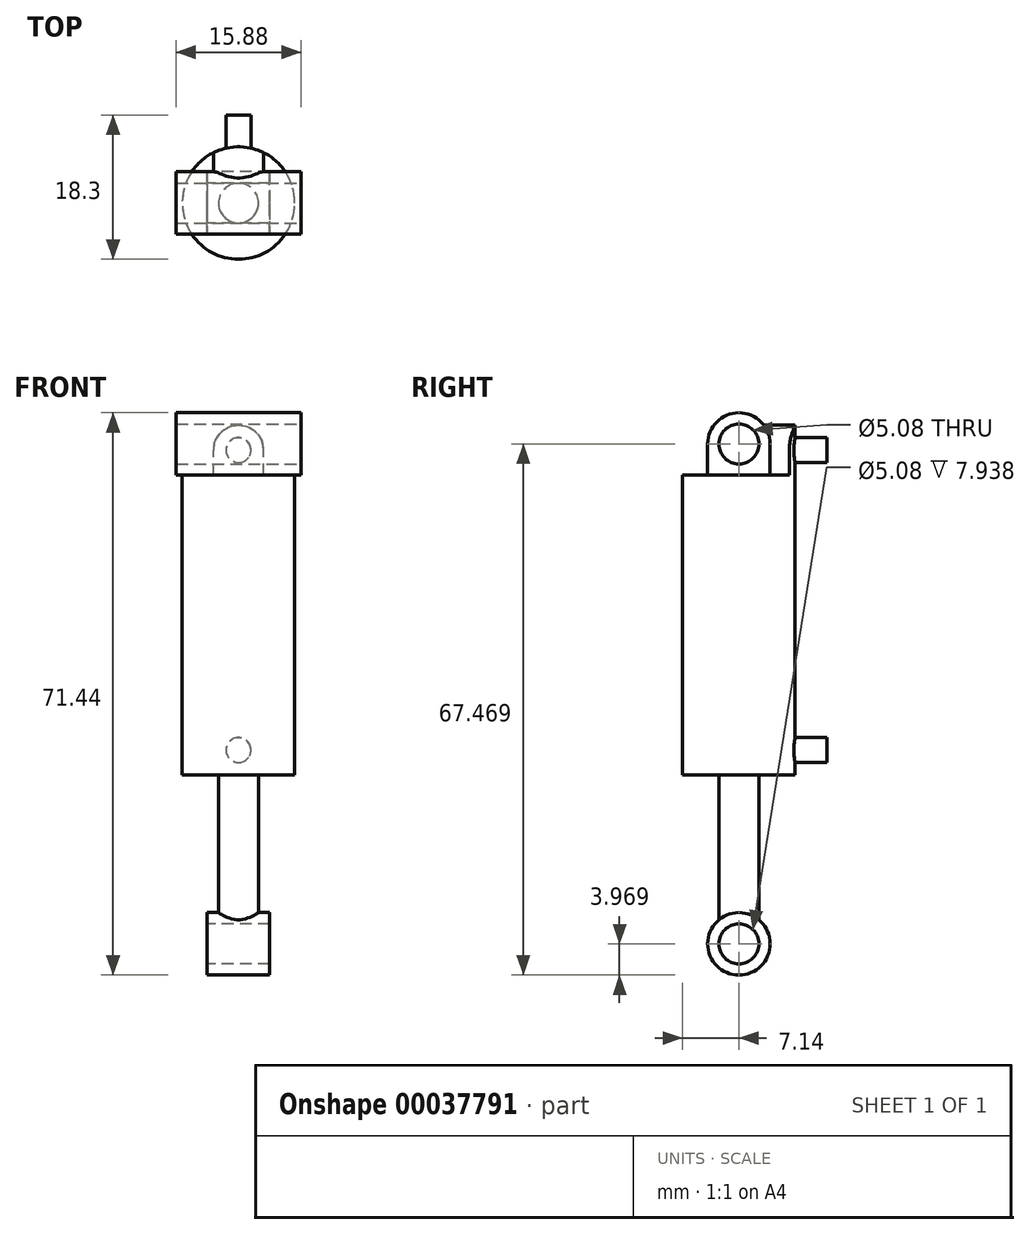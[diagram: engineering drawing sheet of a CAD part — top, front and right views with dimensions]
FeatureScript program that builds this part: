
annotation { "Feature Type Name" : "Feature", "Feature Type Description" : "" }
export const myFeature = defineFeature(function(context is Context, id is Id, definition is map)
    precondition{}
    {
        {
            var Q0;
            Q0=qCreatedBy(makeId("Top.planeOp"),FACE);
            var sketch = newSketch(context, id + "F0", { "sketchPlane" : qUnion([Q0])});
            skCircle(sketch, "E0", {"center": v(0, 0) * mm, "radius": 7.14 * mm});
            skSolve(sketch);
        }
        {
            var Q0;
            Q0 = qSketchRegion(id + "F0", true);
            extrude(context, id + "F1", {"entities" : qUnion([Q0]), "depth" : 38.1 * mm});
        }
        {
            var Q0;
            Q0=makeQuery(id+"F1.opExtrude","CAP_FACE",FACE,{"disambiguationData":[OSD([sQuery(id+"F0.wireOp",EDGE,"E0")])],"isStart":false});
            var sketch = newSketch(context, id + "F2", { "sketchPlane" : qUnion([Q0])});
            skLineSegment(sketch, "E1.rect.bottom", {"start": v(7.94, 3.97) * mm, "end": v(-7.94, 3.97) * mm});
            skLineSegment(sketch, "E1.rect.top", {"start": v(7.94, -3.97) * mm, "end": v(-7.94, -3.97) * mm});
            skLineSegment(sketch, "E1.rect.left", {"start": v(7.94, 3.97) * mm, "end": v(7.94, -3.97) * mm});
            skLineSegment(sketch, "E1.rect.right", {"start": v(-7.94, 3.97) * mm, "end": v(-7.94, -3.97) * mm});
            skPoint(sketch, "E1.rect.middle", {"position": v(0, 0) * mm});
            skSolve(sketch);
        }
        {
            var Q0;
            Q0 = qSketchRegion(id + "F2", true);
            extrude(context, id + "F3", {"entities" : qUnion([Q0]), "operationType" : NewBodyOperationType.ADD, "depth" : 7.94 * mm});
        }
        {
            var Q0;
            Q0=makeQuery(id+"F3.opExtrude","CAP_EDGE",EDGE,{"disambiguationData":[OSD([sQuery(id+"F2.wireOp",EDGE,"E1.rect.bottom")])],"isStart":false});
            var Q1;
            Q1=makeQuery(id+"F3.opExtrude","CAP_EDGE",EDGE,{"disambiguationData":[OSD([sQuery(id+"F2.wireOp",EDGE,"E1.rect.top")])],"isStart":false});
            fillet(context, id + "F4", {"entities" : qUnion([Q0, Q1]), "radius" : 3.97 * mm, "tangentPropagation" : true, "allowEdgeOverflow" : false});
        }
        {
            var Q0;
            Q0=makeQuery(id+"F3.opExtrude","SWEPT_FACE",FACE,{"disambiguationData":[OSD([sQuery(id+"F2.wireOp",EDGE,"E1.rect.left")])]});
            var sketch = newSketch(context, id + "F5", { "sketchPlane" : qUnion([Q0])});
            skCircle(sketch, "E2", {"center": v(0, 42.07) * mm, "radius": 2.54 * mm});
            skSolve(sketch);
        }
        {
            var Q0;
            Q0 = qSketchRegion(id + "F5", true);
            var Q1;
            Q1=makeQuery(id+"F3.opExtrude","SWEPT_FACE",FACE,{"disambiguationData":[OSD([sQuery(id+"F2.wireOp",EDGE,"E1.rect.right")])]});
            extrude(context, id + "F6", {"entities" : qUnion([Q0]), "operationType" : NewBodyOperationType.REMOVE, "endBound" : BoundingType.UP_TO_SURFACE, "oppositeDirection" : true, "endBoundEntityFace" : qUnion([Q1]), "depth" : 25.4 * mm});
        }
        {
            var Q0;
            Q0=makeQuery(id+"F3.opExtrude","SWEPT_FACE",FACE,{"disambiguationData":[OSD([sQuery(id+"F2.wireOp",EDGE,"E1.rect.bottom")])]});
            var sketch = newSketch(context, id + "F7", { "sketchPlane" : qUnion([Q0])});
            skLineSegment(sketch, "E3.bottom", {"start": v(-3.18, 38.1) * mm, "end": v(3.18, 38.1) * mm});
            skLineSegment(sketch, "E3.top", {"start": v(-3.18, 41.27) * mm, "end": v(3.17, 41.27) * mm});
            skLineSegment(sketch, "E3.left", {"start": v(-3.18, 38.1) * mm, "end": v(-3.18, 41.27) * mm});
            skLineSegment(sketch, "E3.right", {"start": v(3.17, 38.1) * mm, "end": v(3.17, 41.27) * mm});
            skPoint(sketch, "E4", {"position": v(0, 38.1) * mm});
            skArc(sketch, "E5", {"start": v(3.17, 41.27) * mm, "mid": v(0, 44.45) * mm, "end": v(-3.18, 41.27) * mm});
            skSolve(sketch);
        }
        {
            var Q0;
            Q0 = qSketchRegion(id + "F7", true);
            var Q1;
            Q1=makeQuery(id+"F1.opExtrude","SWEPT_FACE",FACE,{"disambiguationData":[OSD([sQuery(id+"F0.wireOp",EDGE,"E0")])]});
            var Q2;
            Q2=makeQuery(id+"F4.opFillet","BLEND_FACE",FACE,{"disambiguationData":[OSD([sQuery(id+"F2.wireOp",EDGE,"E1.rect.bottom")])]});
            extrude(context, id + "F8", {"entities" : qUnion([Q0]), "operationType" : NewBodyOperationType.ADD, "endBound" : BoundingType.UP_TO_SURFACE, "endBoundEntityFace" : qUnion([Q1]), "depth" : 25.4 * mm, "hasSecondDirection" : true, "secondDirectionBound" : SecondDirectionBoundingType.UP_TO_SURFACE, "secondDirectionOppositeDirection" : true, "secondDirectionBoundEntityFace" : qUnion([Q2]), "secondDirectionDepth" : 25.4 * mm});
        }
        {
            var Q0;
            Q0=qCreatedBy(makeId("Front.planeOp"),FACE);
            cPlane(context, id + "F9", {"entities" : qUnion([Q0]), "cplaneType" : CPlaneType.OFFSET, "offset" : 6.4 * mm, "oppositeDirection" : true, "width" : 152.4 * mm, "height" : 152.4 * mm});
        }
        {
            var Q0;
            Q0=qCreatedBy(id+"F9.planeOp",FACE);
            var sketch = newSketch(context, id + "F10", { "sketchPlane" : qUnion([Q0])});
            skCircle(sketch, "E6", {"center": v(0, 41.27) * mm, "radius": 1.59 * mm});
            skLineSegment(sketch, "E7", {"start": v(0, 41.27) * mm, "end": v(0, 3.18) * mm, "construction": true});
            skLineSegment(sketch, "E8", {"start": v(0, 3.18) * mm, "end": v(0, 0) * mm, "construction": true});
            skCircle(sketch, "E9", {"center": v(0, 3.18) * mm, "radius": 1.59 * mm});
            skSolve(sketch);
        }
        {
            var Q0;
            Q0 = qSketchRegion(id + "F10", true);
            extrude(context, id + "F11", {"entities" : qUnion([Q0]), "operationType" : NewBodyOperationType.ADD, "oppositeDirection" : true, "depth" : 4.76 * mm});
        }
        {
            var Q0;
            Q0=makeQuery(id+"F1.opExtrude","CAP_FACE",FACE,{"disambiguationData":[OSD([sQuery(id+"F0.wireOp",EDGE,"E0")])],"isStart":true});
            var sketch = newSketch(context, id + "F12", { "sketchPlane" : qUnion([Q0])});
            skCircle(sketch, "E10", {"center": v(0, 0) * mm, "radius": 2.54 * mm});
            skSolve(sketch);
        }
        {
            var Q0;
            Q0 = qSketchRegion(id + "F12", true);
            extrude(context, id + "F13", {"entities" : qUnion([Q0]), "operationType" : NewBodyOperationType.ADD, "depth" : 17.46 * mm});
        }
        {
            var Q0;
            Q0=makeQuery(id+"F13.opExtrude","CAP_FACE",FACE,{"disambiguationData":[OSD([sQuery(id+"F12.wireOp",EDGE,"E10")])],"isStart":false});
            var sketch = newSketch(context, id + "F14", { "sketchPlane" : qUnion([Q0])});
            skLineSegment(sketch, "E11.rect.bottom", {"start": v(3.97, 3.97) * mm, "end": v(-3.97, 3.97) * mm});
            skLineSegment(sketch, "E11.rect.top", {"start": v(3.97, -3.97) * mm, "end": v(-3.97, -3.97) * mm});
            skLineSegment(sketch, "E11.rect.left", {"start": v(3.97, 3.97) * mm, "end": v(3.97, -3.97) * mm});
            skLineSegment(sketch, "E11.rect.right", {"start": v(-3.97, 3.97) * mm, "end": v(-3.97, -3.97) * mm});
            skPoint(sketch, "E11.rect.middle", {"position": v(0, 0) * mm});
            skSolve(sketch);
        }
        {
            var Q0;
            Q0 = qSketchRegion(id + "F14", true);
            extrude(context, id + "F15", {"entities" : qUnion([Q0]), "operationType" : NewBodyOperationType.ADD, "depth" : 7.94 * mm});
        }
        {
            var Q0;
            Q0=makeQuery(id+"F15.opExtrude","CAP_EDGE",EDGE,{"disambiguationData":[OSD([sQuery(id+"F14.wireOp",EDGE,"E11.rect.top")])],"isStart":true});
            var Q1;
            Q1=makeQuery(id+"F15.opExtrude","CAP_EDGE",EDGE,{"disambiguationData":[OSD([sQuery(id+"F14.wireOp",EDGE,"E11.rect.top")])],"isStart":false});
            var Q2;
            Q2=makeQuery(id+"F15.opExtrude","CAP_EDGE",EDGE,{"disambiguationData":[OSD([sQuery(id+"F14.wireOp",EDGE,"E11.rect.bottom")])],"isStart":false});
            var Q3;
            Q3=makeQuery(id+"F15.opExtrude","CAP_EDGE",EDGE,{"disambiguationData":[OSD([sQuery(id+"F14.wireOp",EDGE,"E11.rect.bottom")])],"isStart":true});
            fillet(context, id + "F16", {"entities" : qUnion([Q0, Q1, Q2, Q3]), "radius" : 3.97 * mm, "tangentPropagation" : true, "allowEdgeOverflow" : false});
        }
        {
            var Q0;
            Q0=makeQuery(id+"F15.opExtrude","SWEPT_FACE",FACE,{"disambiguationData":[OSD([sQuery(id+"F14.wireOp",EDGE,"E11.rect.right")])]});
            var sketch = newSketch(context, id + "F17", { "sketchPlane" : qUnion([Q0])});
            skCircle(sketch, "E12", {"center": v(0, -21.43) * mm, "radius": 2.54 * mm});
            skSolve(sketch);
        }
        {
            var Q0;
            Q0 = qSketchRegion(id + "F17", true);
            var Q1;
            Q1=makeQuery(id+"F15.opExtrude","SWEPT_FACE",FACE,{"disambiguationData":[OSD([sQuery(id+"F14.wireOp",EDGE,"E11.rect.left")])]});
            extrude(context, id + "F18", {"entities" : qUnion([Q0]), "operationType" : NewBodyOperationType.REMOVE, "endBound" : BoundingType.UP_TO_SURFACE, "oppositeDirection" : true, "endBoundEntityFace" : qUnion([Q1]), "depth" : 25.4 * mm});
        }
    });
